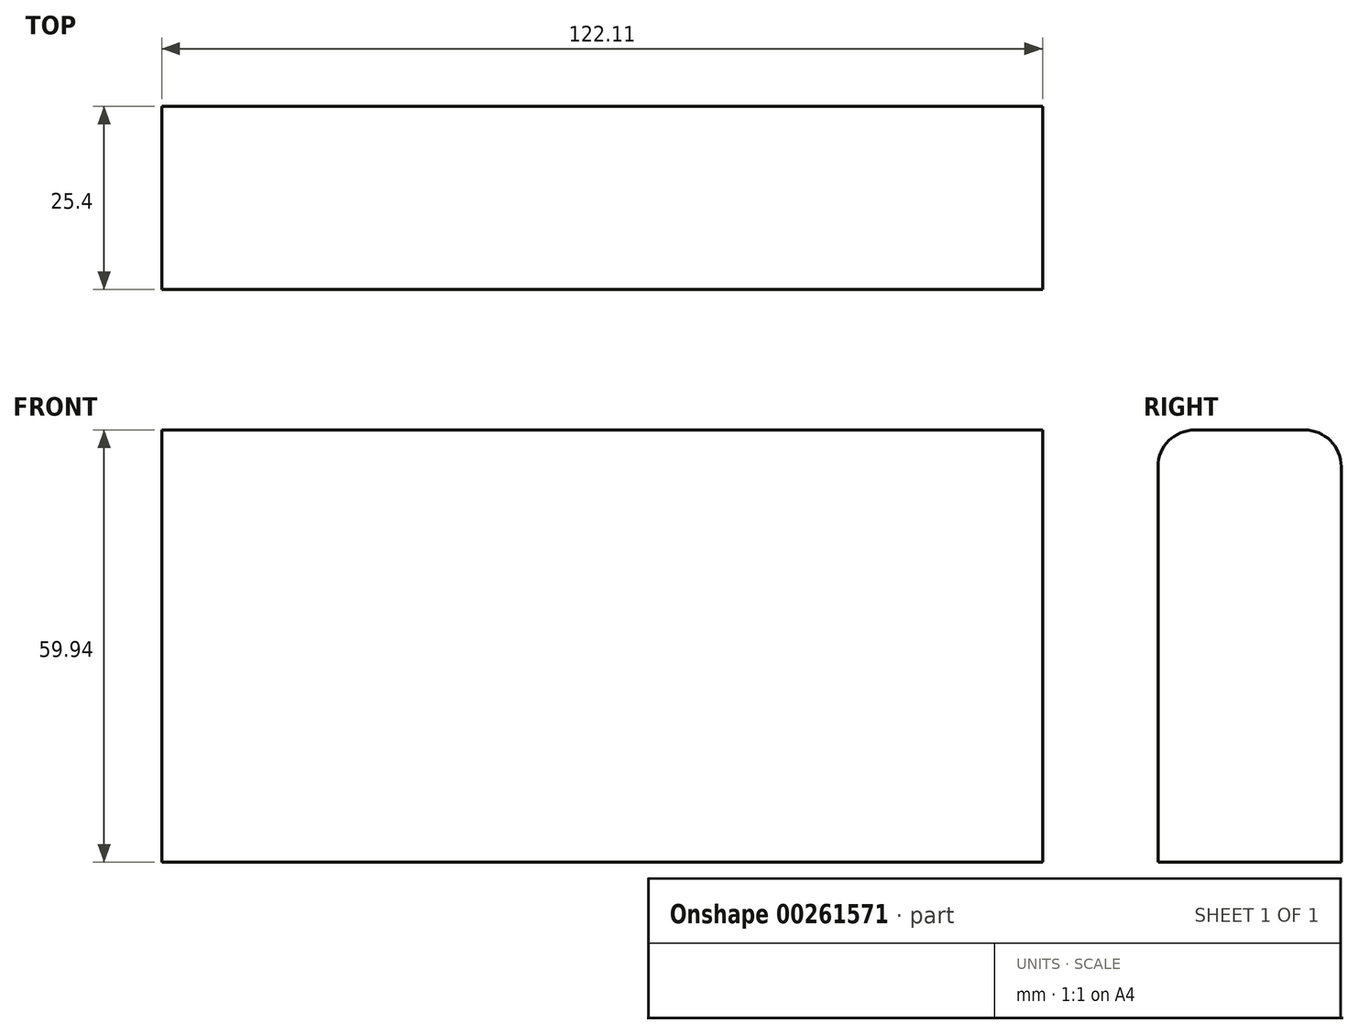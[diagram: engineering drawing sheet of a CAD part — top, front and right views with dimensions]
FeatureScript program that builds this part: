
annotation { "Feature Type Name" : "Feature", "Feature Type Description" : "" }
export const myFeature = defineFeature(function(context is Context, id is Id, definition is map)
    precondition{}
    {
        {
            var Q0;
            Q0=qCreatedBy(makeId("Front.planeOp"),FACE);
            var sketch = newSketch(context, id + "F0", { "sketchPlane" : qUnion([Q0])});
            skLineSegment(sketch, "E0.bottom", {"start": v(34.47, -8.76) * mm, "end": v(-87.64, -8.76) * mm});
            skLineSegment(sketch, "E0.top", {"start": v(34.47, 51.18) * mm, "end": v(-87.64, 51.18) * mm});
            skLineSegment(sketch, "E0.left", {"start": v(34.47, -8.76) * mm, "end": v(34.47, 51.18) * mm});
            skLineSegment(sketch, "E0.right", {"start": v(-87.64, -8.76) * mm, "end": v(-87.64, 51.18) * mm});
            skPoint(sketch, "E0.middle", {"position": v(-26.59, 21.2) * mm});
            skSolve(sketch);
        }
        {
            var Q0;
            Q0=makeQuery(id+"F0.imprint","IMPRINT",FACE,{"disambiguationData":[TD([[makeQuery(id+"F0.imprint","IMPRINT",EDGE,{"derivedFrom":sQuery(id+"F0.wireOp",EDGE,"E0.bottom")}),-1.0]])]});
            extrude(context, id + "F1", {"entities" : qUnion([Q0]), "depth" : 25.4 * mm});
        }
        {
            var Q0;
            Q0=makeQuery(id+"F1.opExtrude","CAP_EDGE",EDGE,{"disambiguationData":[OSD([sQuery(id+"F0.wireOp",EDGE,"E0.top")])],"isStart":false});
            var Q1;
            Q1=makeQuery(id+"F1.opExtrude","CAP_EDGE",EDGE,{"disambiguationData":[OSD([sQuery(id+"F0.wireOp",EDGE,"E0.top")])],"isStart":true});
            fillet(context, id + "F2", {"entities" : qUnion([Q0, Q1]), "radius" : 5.08 * mm, "tangentPropagation" : true, "allowEdgeOverflow" : false});
        }
    });
